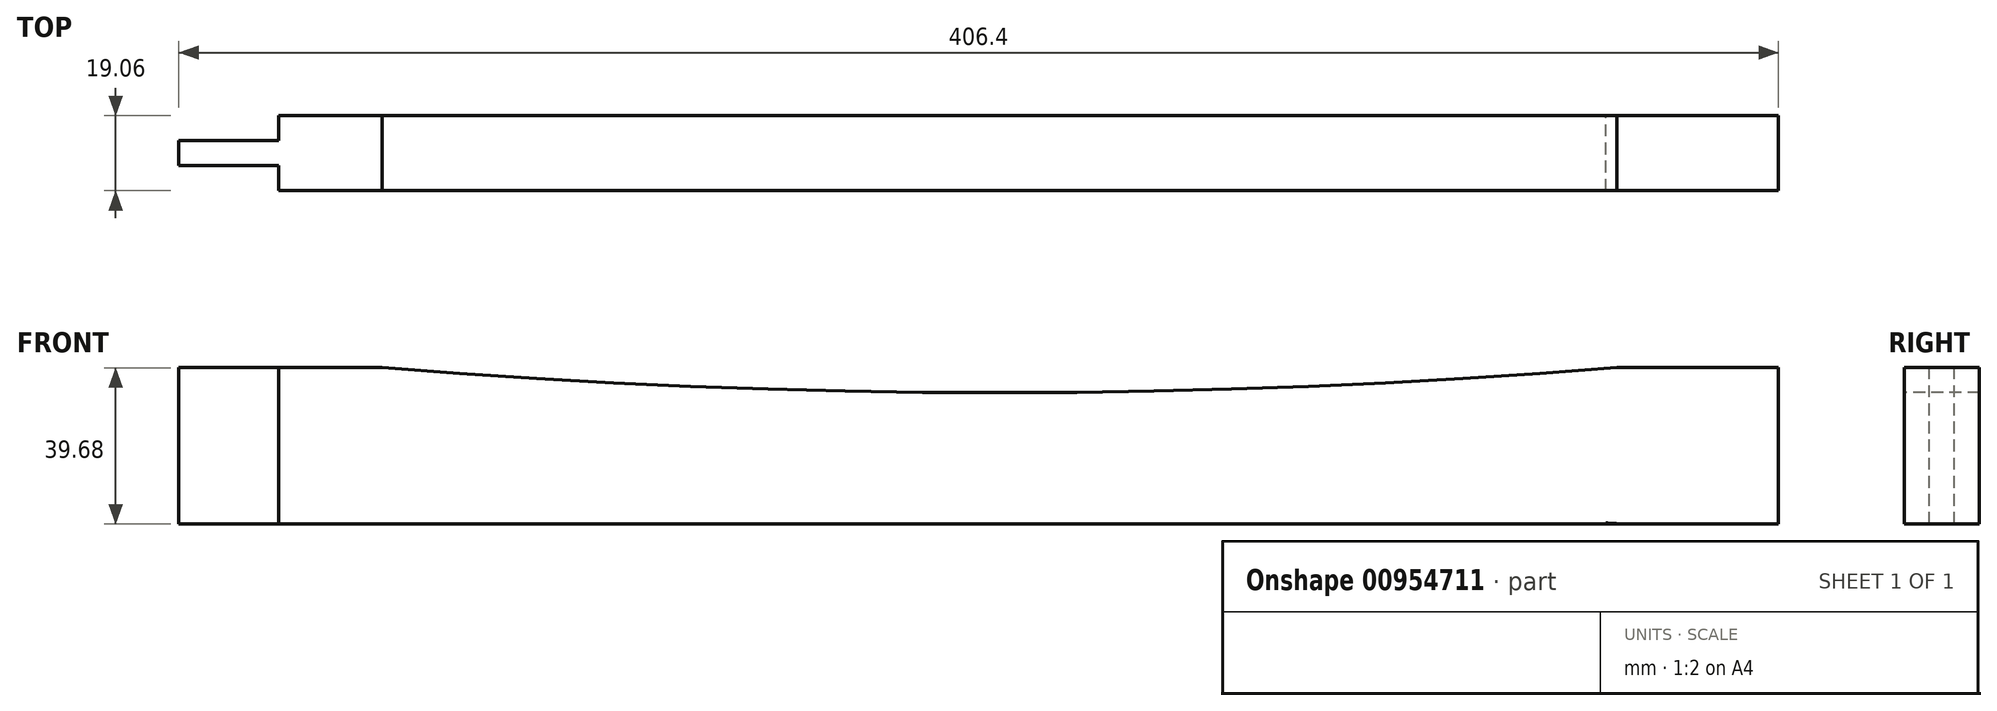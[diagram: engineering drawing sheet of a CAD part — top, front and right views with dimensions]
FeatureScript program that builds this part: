
annotation { "Feature Type Name" : "Feature", "Feature Type Description" : "" }
export const myFeature = defineFeature(function(context is Context, id is Id, definition is map)
    precondition{}
    {
        {
            var Q0;
            Q0=qCreatedBy(makeId("Front.planeOp"),FACE);
            var sketch = newSketch(context, id + "F0", { "sketchPlane" : qUnion([Q0])});
            skLineSegment(sketch, "E0", {"start": v(203.2, 0) * mm, "end": v(-203.2, 0) * mm, "construction": true});
            skLineSegment(sketch, "E1", {"start": v(0, -19.84) * mm, "end": v(0, 19.84) * mm, "construction": true});
            skLineSegment(sketch, "E2.bottom", {"start": v(-203.2, -19.84) * mm, "end": v(203.2, -19.84) * mm});
            skLineSegment(sketch, "E2.top", {"start": v(-203.2, 19.84) * mm, "end": v(203.2, 19.84) * mm});
            skLineSegment(sketch, "E2.left", {"start": v(-203.2, -19.84) * mm, "end": v(-203.2, 19.84) * mm});
            skLineSegment(sketch, "E2.right", {"start": v(203.2, -19.84) * mm, "end": v(203.2, 19.84) * mm});
            skSolve(sketch);
        }
        {
            var Q0;
            Q0 = qSketchRegion(id + "F0", true);
            extrude(context, id + "F1", {"entities" : qUnion([Q0]), "endBound" : BoundingType.SYMMETRIC, "depth" : 19.05 * mm, "offsetDistance" : 25 * mm});
        }
        {
            var Q0;
            Q0=makeQuery(id+"F1.opExtrude","SWEPT_FACE",FACE,{"disambiguationData":[OSD([sQuery(id+"F0.wireOp",EDGE,"E2.top")])]});
            var sketch = newSketch(context, id + "F2", { "sketchPlane" : qUnion([Q0])});
            skLineSegment(sketch, "E3", {"start": v(0, 108.09) * mm, "end": v(0, -107) * mm, "construction": true});
            skLineSegment(sketch, "E4", {"start": v(177.8, 9.53) * mm, "end": v(177.8, -9.52) * mm, "construction": true});
            skLineSegment(sketch, "E5.0", {"start": v(-203.2, -9.53) * mm, "end": v(203.2, -9.53) * mm});
            skLineSegment(sketch, "E6.0", {"start": v(-203.2, 9.53) * mm, "end": v(203.2, 9.53) * mm});
            skLineSegment(sketch, "E7.0", {"start": v(203.2, -9.53) * mm, "end": v(203.2, 9.52) * mm});
            skLineSegment(sketch, "E8", {"start": v(177.8, 3.18) * mm, "end": v(203.2, 3.18) * mm});
            skLineSegment(sketch, "E9", {"start": v(203.2, -3.17) * mm, "end": v(177.8, -3.17) * mm});
            skLineSegment(sketch, "E10", {"start": v(203.2, 0) * mm, "end": v(0, 0) * mm, "construction": true});
            skLineSegment(sketch, "E11.bottom", {"start": v(203.2, 9.53) * mm, "end": v(177.8, 9.53) * mm});
            skLineSegment(sketch, "E11.top", {"start": v(203.2, 3.18) * mm, "end": v(177.8, 3.18) * mm});
            skLineSegment(sketch, "E11.left", {"start": v(203.2, 9.53) * mm, "end": v(203.2, 3.18) * mm});
            skLineSegment(sketch, "E11.right", {"start": v(177.8, 9.53) * mm, "end": v(177.8, 3.18) * mm});
            skLineSegment(sketch, "E12.bottom", {"start": v(203.2, -9.53) * mm, "end": v(177.8, -9.53) * mm});
            skLineSegment(sketch, "E12.left", {"start": v(203.2, -9.53) * mm, "end": v(203.2, -3.17) * mm});
            skLineSegment(sketch, "E12.right", {"start": v(177.8, -9.53) * mm, "end": v(177.8, -3.17) * mm});
            skLineSegment(sketch, "E13.MirrorCS", {"start": v(-203.2, -3.17) * mm, "end": v(-177.8, -3.17) * mm});
            skLineSegment(sketch, "E14.MirrorCS", {"start": v(-177.8, 3.18) * mm, "end": v(-203.2, 3.18) * mm});
            skLineSegment(sketch, "E15", {"start": v(-177.8, 3.18) * mm, "end": v(-177.8, 9.53) * mm});
            skLineSegment(sketch, "E16", {"start": v(-177.8, -3.17) * mm, "end": v(-177.8, -9.53) * mm});
            skSolve(sketch);
        }
        {
            var Q0;
            Q0=makeQuery(id+"F2.imprint","IMPRINT",FACE,{"disambiguationData":[TD([[makeQuery(id+"F2.imprint","IMPRINT",EDGE,{"derivedFrom":sQuery(id+"F2.wireOp",EDGE,"E12.bottom")}),1.0]])]});
            var Q1;
            Q1=makeQuery(id+"F2.imprint","IMPRINT",FACE,{"disambiguationData":[TD([[makeQuery(id+"F2.imprint","IMPRINT",EDGE,{"derivedFrom":sQuery(id+"F2.wireOp",EDGE,"E11.bottom")}),-1.0]])]});
            var Q2;
            {var subQ4=sQuery(id+"F2.wireOp",EDGE,"E13.MirrorCS");Q2=makeQuery(id+"F2.imprint","IMPRINT",FACE,{"disambiguationData":[TD([[makeQuery(id+"F2.imprint","IMPRINT",EDGE,{"derivedFrom":subQ4}),-1.0]])]});}
            var Q3;
            {var subQ4=sQuery(id+"F2.wireOp",EDGE,"E14.MirrorCS");Q3=makeQuery(id+"F2.imprint","IMPRINT",FACE,{"disambiguationData":[TD([[makeQuery(id+"F2.imprint","IMPRINT",EDGE,{"derivedFrom":subQ4}),-1.0]])]});}
            extrude(context, id + "F3", {"entities" : qUnion([Q0, Q1, Q2, Q3]), "operationType" : NewBodyOperationType.REMOVE, "endBound" : BoundingType.THROUGH_ALL, "oppositeDirection" : true, "depth" : 25 * mm, "offsetDistance" : 25 * mm});
        }
        {
            var Q0;
            Q0=makeQuery(id+"F1.opExtrude","CAP_FACE",FACE,{"disambiguationData":[OSD([sQuery(id+"F0.wireOp",EDGE,"E2.bottom"),sQuery(id+"F0.wireOp",EDGE,"E2.top"),sQuery(id+"F0.wireOp",EDGE,"E2.left"),sQuery(id+"F0.wireOp",EDGE,"E2.right")])],"isStart":false});
            var sketch = newSketch(context, id + "F4", { "sketchPlane" : qUnion([Q0])});
            skLineSegment(sketch, "E17", {"start": v(-165.1, 19.84) * mm, "end": v(-165.1, -19.84) * mm, "construction": true});
            skLineSegment(sketch, "E18.0", {"start": v(-177.8, -19.84) * mm, "end": v(-177.8, 19.84) * mm});
            skLineSegment(sketch, "E19.0", {"start": v(177.8, -19.84) * mm, "end": v(177.8, 19.84) * mm});
            skLineSegment(sketch, "E20.0", {"start": v(-177.8, -19.84) * mm, "end": v(177.8, -19.84) * mm});
            skLineSegment(sketch, "E21.0", {"start": v(-177.8, 19.84) * mm, "end": v(177.8, 19.84) * mm});
            skArc(sketch, "E22", {"start": v(-165.1, 19.84) * mm, "mid": v(-177.8, 0) * mm, "end": v(-165.1, -19.84) * mm});
            skLineSegment(sketch, "E23", {"start": v(165.1, 19.84) * mm, "end": v(165.1, -19.84) * mm, "construction": true});
            skArc(sketch, "E24", {"start": v(165.1, -19.84) * mm, "mid": v(177.8, 0) * mm, "end": v(165.1, 19.84) * mm});
            skLineSegment(sketch, "E25", {"start": v(-165.1, 13.5) * mm, "end": v(165.1, 13.5) * mm, "construction": true});
            skLineSegment(sketch, "E26", {"start": v(0, 0) * mm, "end": v(-155.95, 0) * mm, "construction": true});
            skLineSegment(sketch, "E27", {"start": v(0, 0) * mm, "end": v(155.95, 0) * mm, "construction": true});
            skLineSegment(sketch, "E28.MirrorCS", {"start": v(-165.1, -13.5) * mm, "end": v(165.1, -13.5) * mm, "construction": true});
            skEllipticalArc(sketch, "E29", {});
            skEllipticalArc(sketch, "E30", {});
            skLineSegment(sketch, "E31", {"start": v(0, 19.84) * mm, "end": v(0, -19.84) * mm, "construction": true});
            skArc(sketch, "E32", {"start": v(-151.49, 19.84) * mm, "mid": v(5.35, 13.5) * mm, "end": v(162.18, 19.84) * mm});
            skArc(sketch, "E33.MirrorCS", {"start": v(-151.49, -19.84) * mm, "mid": v(5.35, -13.5) * mm, "end": v(162.18, -19.84) * mm});
            skEllipticalArc(sketch, "E34.trimOffspring", {});
            skEllipticalArc(sketch, "E35.trimOffspring", {});
            const initialGuessF4  = {"E29": [0.1651, 0, -1, 0, 0.0381, 0.01984375, 1.4190725383668028, 1.5707963267948966], "E30": [-0.1559470703125, 0, -1, 0, 0.047252929687500014, 0.01984375, 1.355708725792563, 1.7564929116828665], "E34.trimOffspring": [-0.1559470703125, 0, -1, 0, 0.047252929687500014, 0.01984375, 4.52669239549672, 4.927476581387025], "E35.trimOffspring": [0.1651, 0, -1, 0, 0.0381, 0.01984375, 4.71238898038469, 4.864112768812779]};
            skSetInitialGuess(sketch, initialGuessF4);
            skSolve(sketch);
        }
        {
            var Q0;
            {var subQ0=sQuery(id+"F4.wireOp",EDGE,"E32");var subQ1=sQuery(id+"F4.wireOp",EDGE,"E21.0");var subQ2=makeQuery(id+"F4.imprint","INTERSECT",VERTEX,{"disambiguationData":[OD(0.0)],"derivedFrom":[subQ1,subQ0]});Q0=makeQuery(id+"F4.imprint","IMPRINT",FACE,{"disambiguationData":[TD([[makeQuery(id+"F4.imprint","IMPRINT",EDGE,{"disambiguationData":[TD([[subQ2,-1.0]])],"derivedFrom":subQ1}),-1.0]])]});}
            var Q1;
            {var subQ0=sQuery(id+"F4.wireOp",EDGE,"E33.MirrorCS");var subQ1=sQuery(id+"F4.wireOp",EDGE,"E20.0");var subQ2=makeQuery(id+"F4.imprint","INTERSECT",VERTEX,{"disambiguationData":[OD(0.0)],"derivedFrom":[subQ1,subQ0]});Q1=makeQuery(id+"F4.imprint","IMPRINT",FACE,{"disambiguationData":[TD([[makeQuery(id+"F4.imprint","IMPRINT",EDGE,{"disambiguationData":[TD([[subQ2,-1.0]])],"derivedFrom":subQ1}),1.0]])]});}
            extrude(context, id + "F5", {"entities" : qUnion([Q0, Q1]), "operationType" : NewBodyOperationType.REMOVE, "endBound" : BoundingType.THROUGH_ALL, "oppositeDirection" : true, "depth" : 25 * mm, "offsetDistance" : 25 * mm});
        }
    });
